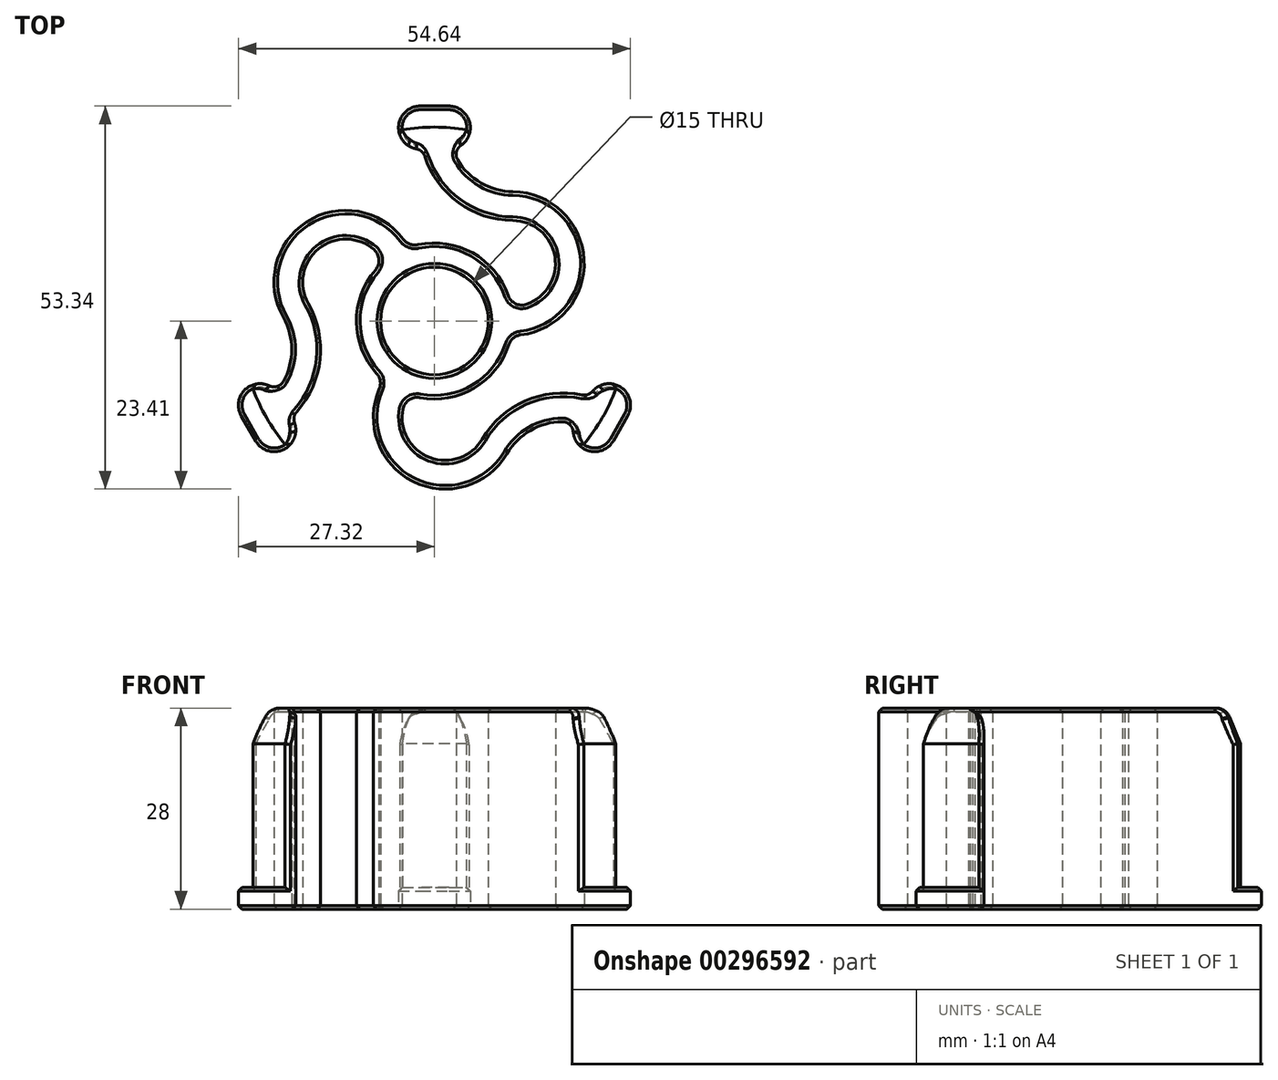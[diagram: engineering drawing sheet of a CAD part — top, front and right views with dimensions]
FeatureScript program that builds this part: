
annotation { "Feature Type Name" : "Feature", "Feature Type Description" : "" }
export const myFeature = defineFeature(function(context is Context, id is Id, definition is map)
    precondition{}
    {
        {
            var Q0;
            Q0=qCreatedBy(makeId("Top.planeOp"),FACE);
            var sketch = newSketch(context, id + "F0", { "sketchPlane" : qUnion([Q0])});
            skCircle(sketch, "E0", {"center": v(0, 0) * mm, "radius": 7.5 * mm});
            skArc(sketch, "E1", {"start": v(10.27, 3.56) * mm, "mid": v(5.32, 9.48) * mm, "end": v(-2.3, 10.62) * mm});
            skCircle(sketch, "E2", {"center": v(0, 0) * mm, "radius": 27 * mm, "construction": true});
            skArc(sketch, "E3", {"start": v(10.87, 0) * mm, "mid": v(18.87, 7.97) * mm, "end": v(10.92, 16) * mm, "construction": true});
            skLineSegment(sketch, "E4", {"start": v(0, 0) * mm, "end": v(0, 27) * mm, "construction": true});
            skArc(sketch, "E5", {"start": v(0, 27) * mm, "mid": v(3.2, 19.25) * mm, "end": v(10.92, 16) * mm, "construction": true});
            skLineSegment(sketch, "E6", {"start": v(10.87, 0) * mm, "end": v(0, 0) * mm, "construction": true});
            skArc(sketch, "E7.0", {"start": v(12.8, 2.32) * mm, "mid": v(16.79, 8.96) * mm, "end": v(10.9, 14) * mm});
            skArc(sketch, "E7.1", {"start": v(-1.36, 22.96) * mm, "mid": v(3.33, 16.5) * mm, "end": v(10.9, 14) * mm});
            skArc(sketch, "E8.0", {"start": v(12.02, -1.93) * mm, "mid": v(20.85, 8.54) * mm, "end": v(10.94, 18) * mm});
            skArc(sketch, "E8.1", {"start": v(3.24, 22.45) * mm, "mid": v(6.5, 19.2) * mm, "end": v(10.94, 18) * mm});
            skLineSegment(sketch, "E9", {"start": v(0, 27) * mm, "end": v(0, 32) * mm, "construction": true});
            skPoint(sketch, "E10.visualSharp", {"position": v(10.68, -2) * mm});
            skArc(sketch, "E10.filletArc", {"start": v(12.02, -1.93) * mm, "mid": v(10.98, -2.38) * mm, "end": v(10.35, -3.31) * mm});
            skPoint(sketch, "E11.visualSharp", {"position": v(10.68, 2) * mm});
            skArc(sketch, "E11.filletArc", {"start": v(10.27, 3.56) * mm, "mid": v(11.28, 2.42) * mm, "end": v(12.8, 2.32) * mm});
            skArc(sketch, "E12", {"start": v(-4.97, 26.54) * mm, "mid": v(-4.17, 24.85) * mm, "end": v(-2.52, 23.97) * mm});
            skArc(sketch, "E13", {"start": v(3.69, 24.45) * mm, "mid": v(4.56, 25.35) * mm, "end": v(4.98, 26.54) * mm});
            skArc(sketch, "E14", {"start": v(4.98, 26.54) * mm, "mid": v(0, 27) * mm, "end": v(-4.97, 26.54) * mm});
            skArc(sketch, "E15.1.0", {"start": v(-4.34, 11.38) * mm, "mid": v(-17.83, 13.79) * mm, "end": v(-21.06, 0.47) * mm});
            skArc(sketch, "E15.1.1", {"start": v(-8.22, 7.11) * mm, "mid": v(-7.73, 8.56) * mm, "end": v(-8.41, 9.93) * mm});
            skArc(sketch, "E15.1.2", {"start": v(-4.34, 11.38) * mm, "mid": v(-3.43, 10.7) * mm, "end": v(-2.3, 10.62) * mm});
            skArc(sketch, "E15.1.3", {"start": v(-8.41, 9.93) * mm, "mid": v(-16.15, 10.06) * mm, "end": v(-17.58, 2.45) * mm});
            skArc(sketch, "E15.1.4", {"start": v(-5.43, 9.41) * mm, "mid": v(-16.34, 12.35) * mm, "end": v(-19.32, 1.46) * mm, "construction": true});
            skArc(sketch, "E15.1.5", {"start": v(-23.38, -13.5) * mm, "mid": v(-18.27, -6.86) * mm, "end": v(-19.32, 1.46) * mm, "construction": true});
            skArc(sketch, "E15.1.6", {"start": v(-21.06, -8.42) * mm, "mid": v(-19.88, -3.97) * mm, "end": v(-21.06, 0.47) * mm});
            skArc(sketch, "E15.1.7", {"start": v(-19.2, -12.65) * mm, "mid": v(-15.96, -5.37) * mm, "end": v(-17.58, 2.45) * mm});
            skArc(sketch, "E15.1.8", {"start": v(-20.5, -17.58) * mm, "mid": v(-19.44, -16.04) * mm, "end": v(-19.5, -14.17) * mm});
            skArc(sketch, "E15.1.9", {"start": v(-23.01, -9.03) * mm, "mid": v(-24.23, -8.73) * mm, "end": v(-25.47, -8.96) * mm});
            skArc(sketch, "E15.1.10", {"start": v(-25.47, -8.96) * mm, "mid": v(-23.38, -13.5) * mm, "end": v(-20.5, -17.58) * mm});
            skArc(sketch, "E15.2.0", {"start": v(-7.69, -9.45) * mm, "mid": v(-3.03, -22.33) * mm, "end": v(10.12, -18.47) * mm});
            skArc(sketch, "E15.2.1", {"start": v(-2.05, -10.67) * mm, "mid": v(-3.55, -10.98) * mm, "end": v(-4.4, -12.25) * mm});
            skArc(sketch, "E15.2.2", {"start": v(-7.69, -9.45) * mm, "mid": v(-7.55, -8.32) * mm, "end": v(-8.04, -7.3) * mm});
            skArc(sketch, "E15.2.3", {"start": v(-4.4, -12.25) * mm, "mid": v(-0.63, -19.02) * mm, "end": v(6.67, -16.45) * mm});
            skArc(sketch, "E15.2.4", {"start": v(-5.43, -9.41) * mm, "mid": v(-2.53, -20.32) * mm, "end": v(8.4, -17.46) * mm, "construction": true});
            skArc(sketch, "E15.2.5", {"start": v(23.38, -13.5) * mm, "mid": v(15.07, -12.4) * mm, "end": v(8.4, -17.46) * mm, "construction": true});
            skArc(sketch, "E15.2.6", {"start": v(17.82, -14.03) * mm, "mid": v(13.38, -15.23) * mm, "end": v(10.12, -18.47) * mm});
            skArc(sketch, "E15.2.7", {"start": v(20.56, -10.3) * mm, "mid": v(12.63, -11.14) * mm, "end": v(6.67, -16.45) * mm});
            skArc(sketch, "E15.2.8", {"start": v(25.47, -8.96) * mm, "mid": v(23.6, -8.82) * mm, "end": v(22.02, -9.8) * mm});
            skArc(sketch, "E15.2.9", {"start": v(19.33, -15.42) * mm, "mid": v(19.68, -16.62) * mm, "end": v(20.5, -17.58) * mm});
            skArc(sketch, "E15.2.10", {"start": v(20.5, -17.58) * mm, "mid": v(23.38, -13.5) * mm, "end": v(25.47, -8.96) * mm});
            skLineSegment(sketch, "E16", {"start": v(-5.43, 9.41) * mm, "end": v(0, 0) * mm, "construction": true});
            skArc(sketch, "E17.trimOffspring", {"start": v(-8.22, 7.11) * mm, "mid": v(-10.87, -0.13) * mm, "end": v(-8.04, -7.3) * mm});
            skArc(sketch, "E18.trimOffspring", {"start": v(-2.05, -10.67) * mm, "mid": v(5.55, -9.34) * mm, "end": v(10.35, -3.31) * mm});
            skPoint(sketch, "E19.visualSharp", {"position": v(-19.92, -13.4) * mm});
            skArc(sketch, "E19.filletArc", {"start": v(-19.2, -12.65) * mm, "mid": v(-19.56, -13.37) * mm, "end": v(-19.5, -14.17) * mm});
            skPoint(sketch, "E20.visualSharp", {"position": v(-22.02, -9.8) * mm});
            skArc(sketch, "E20.filletArc", {"start": v(-23.01, -9.03) * mm, "mid": v(-21.92, -9.11) * mm, "end": v(-21.06, -8.42) * mm});
            skPoint(sketch, "E21.visualSharp", {"position": v(-1.64, 23.95) * mm});
            skArc(sketch, "E21.filletArc", {"start": v(-1.36, 22.96) * mm, "mid": v(-1.8, 23.63) * mm, "end": v(-2.52, 23.97) * mm});
            skPoint(sketch, "E22.visualSharp", {"position": v(2.52, 23.97) * mm});
            skArc(sketch, "E22.filletArc", {"start": v(3.69, 24.45) * mm, "mid": v(3.07, 23.53) * mm, "end": v(3.24, 22.45) * mm});
            skPoint(sketch, "E23.visualSharp", {"position": v(21.56, -10.56) * mm});
            skArc(sketch, "E23.filletArc", {"start": v(20.56, -10.3) * mm, "mid": v(21.36, -10.26) * mm, "end": v(22.02, -9.8) * mm});
            skPoint(sketch, "E24.visualSharp", {"position": v(19.5, -14.17) * mm});
            skArc(sketch, "E24.filletArc", {"start": v(19.33, -15.42) * mm, "mid": v(18.85, -14.42) * mm, "end": v(17.82, -14.03) * mm});
            skSolve(sketch);
        }
        {
            var Q0;
            Q0 = qSketchRegion(id + "F0", true);
            extrude(context, id + "F1", {"entities" : qUnion([Q0]), "depth" : 28 * mm});
        }
        {
            var Q0;
            Q0=makeQuery(id+"F1.opExtrude","CAP_FACE",FACE,{"disambiguationData":[OSD([sQuery(id+"F0.wireOp",EDGE,"E0"),sQuery(id+"F0.wireOp",EDGE,"E1"),sQuery(id+"F0.wireOp",EDGE,"E7.0"),sQuery(id+"F0.wireOp",EDGE,"E7.1"),sQuery(id+"F0.wireOp",EDGE,"E8.0"),sQuery(id+"F0.wireOp",EDGE,"E8.1"),sQuery(id+"F0.wireOp",EDGE,"E10.filletArc"),sQuery(id+"F0.wireOp",EDGE,"E11.filletArc"),sQuery(id+"F0.wireOp",EDGE,"E12"),sQuery(id+"F0.wireOp",EDGE,"E13"),sQuery(id+"F0.wireOp",EDGE,"E14"),sQuery(id+"F0.wireOp",EDGE,"E15.1.0"),sQuery(id+"F0.wireOp",EDGE,"E15.1.1"),sQuery(id+"F0.wireOp",EDGE,"E15.1.2"),sQuery(id+"F0.wireOp",EDGE,"E15.1.3"),sQuery(id+"F0.wireOp",EDGE,"E15.1.6"),sQuery(id+"F0.wireOp",EDGE,"E15.1.7"),sQuery(id+"F0.wireOp",EDGE,"E15.1.8"),sQuery(id+"F0.wireOp",EDGE,"E15.1.9"),sQuery(id+"F0.wireOp",EDGE,"E15.1.10"),sQuery(id+"F0.wireOp",EDGE,"E15.2.0"),sQuery(id+"F0.wireOp",EDGE,"E15.2.1"),sQuery(id+"F0.wireOp",EDGE,"E15.2.2"),sQuery(id+"F0.wireOp",EDGE,"E15.2.3"),sQuery(id+"F0.wireOp",EDGE,"E15.2.6"),sQuery(id+"F0.wireOp",EDGE,"E15.2.7"),sQuery(id+"F0.wireOp",EDGE,"E15.2.8"),sQuery(id+"F0.wireOp",EDGE,"E15.2.9"),sQuery(id+"F0.wireOp",EDGE,"E15.2.10"),sQuery(id+"F0.wireOp",EDGE,"E17.trimOffspring"),sQuery(id+"F0.wireOp",EDGE,"E18.trimOffspring")])],"isStart":true});
            var sketch = newSketch(context, id + "F2", { "sketchPlane" : qUnion([Q0])});
            skArc(sketch, "E25", {"start": v(-2, -23.93) * mm, "mid": v(-5, -26.93) * mm, "end": v(-2, -29.93) * mm});
            skArc(sketch, "E26", {"start": v(2, -29.93) * mm, "mid": v(5, -26.93) * mm, "end": v(2, -23.93) * mm});
            skLineSegment(sketch, "E27", {"start": v(-2, -29.93) * mm, "end": v(2, -29.93) * mm});
            skLineSegment(sketch, "E28", {"start": v(-2, -23.93) * mm, "end": v(2, -23.93) * mm});
            skLineSegment(sketch, "E29.1.0", {"start": v(26.92, 13.23) * mm, "end": v(24.92, 16.7) * mm});
            skLineSegment(sketch, "E29.1.1", {"start": v(21.72, 10.23) * mm, "end": v(19.72, 13.7) * mm});
            skArc(sketch, "E29.1.2", {"start": v(24.92, 16.7) * mm, "mid": v(20.82, 17.8) * mm, "end": v(19.72, 13.7) * mm});
            skArc(sketch, "E29.1.3", {"start": v(21.72, 10.23) * mm, "mid": v(25.82, 9.13) * mm, "end": v(26.92, 13.23) * mm});
            skLineSegment(sketch, "E29.2.0", {"start": v(-24.92, 16.7) * mm, "end": v(-26.92, 13.23) * mm});
            skLineSegment(sketch, "E29.2.1", {"start": v(-19.72, 13.7) * mm, "end": v(-21.72, 10.23) * mm});
            skArc(sketch, "E29.2.2", {"start": v(-26.92, 13.23) * mm, "mid": v(-25.82, 9.13) * mm, "end": v(-21.72, 10.23) * mm});
            skArc(sketch, "E29.2.3", {"start": v(-19.72, 13.7) * mm, "mid": v(-20.82, 17.8) * mm, "end": v(-24.92, 16.7) * mm});
            skPoint(sketch, "E29.center", {"position": v(0, 0) * mm});
            skLineSegment(sketch, "E30", {"start": v(0, 0) * mm, "end": v(-24.32, 11.73) * mm, "construction": true});
            skSolve(sketch);
        }
        {
            var Q0;
            Q0 = qSketchRegion(id + "F2", true);
            extrude(context, id + "F3", {"entities" : qUnion([Q0]), "operationType" : NewBodyOperationType.ADD, "oppositeDirection" : true, "depth" : 3 * mm});
        }
        {
            var Q0;
            Q0=makeQuery(id+"F1.opExtrude","CAP_EDGE",EDGE,{"disambiguationData":[OSD([sQuery(id+"F0.wireOp",EDGE,"E15.2.10")])],"isStart":false});
            var Q1;
            Q1=makeQuery(id+"F1.opExtrude","CAP_EDGE",EDGE,{"disambiguationData":[OSD([sQuery(id+"F0.wireOp",EDGE,"E15.1.10")])],"isStart":false});
            var Q2;
            Q2=makeQuery(id+"F1.opExtrude","CAP_EDGE",EDGE,{"disambiguationData":[OSD([sQuery(id+"F0.wireOp",EDGE,"E14")])],"isStart":false});
            chamfer(context, id + "F4", {"entities" : qUnion([Q0, Q1, Q2]), "chamferType" : ChamferType.TWO_OFFSETS, "width1" : 2 * mm, "oppositeDirection" : false, "width2" : 5 * mm, "tangentPropagation" : true});
        }
        {
            var Q0;
            {var subQ0=sQuery(id+"F0.wireOp",EDGE,"E15.2.10");Q0=makeQuery(id+"F4.opChamfer","BLEND_EDGE",EDGE,{"blendedFrom":[makeQuery(id+"F1.opExtrude","CAP_EDGE",EDGE,{"disambiguationData":[OSD([subQ0])],"isStart":false}),makeQuery(id+"F1.opExtrude","CAP_FACE",FACE,{"disambiguationData":[OSD([sQuery(id+"F0.wireOp",EDGE,"E0"),sQuery(id+"F0.wireOp",EDGE,"E1"),sQuery(id+"F0.wireOp",EDGE,"E7.0"),sQuery(id+"F0.wireOp",EDGE,"E7.1"),sQuery(id+"F0.wireOp",EDGE,"E8.0"),sQuery(id+"F0.wireOp",EDGE,"E8.1"),sQuery(id+"F0.wireOp",EDGE,"E10.filletArc"),sQuery(id+"F0.wireOp",EDGE,"E11.filletArc"),sQuery(id+"F0.wireOp",EDGE,"E12"),sQuery(id+"F0.wireOp",EDGE,"E13"),sQuery(id+"F0.wireOp",EDGE,"E14"),sQuery(id+"F0.wireOp",EDGE,"E15.1.0"),sQuery(id+"F0.wireOp",EDGE,"E15.1.1"),sQuery(id+"F0.wireOp",EDGE,"E15.1.2"),sQuery(id+"F0.wireOp",EDGE,"E15.1.3"),sQuery(id+"F0.wireOp",EDGE,"E15.1.6"),sQuery(id+"F0.wireOp",EDGE,"E15.1.7"),sQuery(id+"F0.wireOp",EDGE,"E15.1.8"),sQuery(id+"F0.wireOp",EDGE,"E15.1.9"),sQuery(id+"F0.wireOp",EDGE,"E15.1.10"),sQuery(id+"F0.wireOp",EDGE,"E15.2.0"),sQuery(id+"F0.wireOp",EDGE,"E15.2.1"),sQuery(id+"F0.wireOp",EDGE,"E15.2.2"),sQuery(id+"F0.wireOp",EDGE,"E15.2.3"),sQuery(id+"F0.wireOp",EDGE,"E15.2.6"),sQuery(id+"F0.wireOp",EDGE,"E15.2.7"),sQuery(id+"F0.wireOp",EDGE,"E15.2.8"),sQuery(id+"F0.wireOp",EDGE,"E15.2.9"),subQ0,sQuery(id+"F0.wireOp",EDGE,"E17.trimOffspring"),sQuery(id+"F0.wireOp",EDGE,"E18.trimOffspring"),sQuery(id+"F0.wireOp",EDGE,"E19.filletArc"),sQuery(id+"F0.wireOp",EDGE,"E20.filletArc"),sQuery(id+"F0.wireOp",EDGE,"E21.filletArc"),sQuery(id+"F0.wireOp",EDGE,"E22.filletArc"),sQuery(id+"F0.wireOp",EDGE,"E23.filletArc"),sQuery(id+"F0.wireOp",EDGE,"E24.filletArc")])],"isStart":false})],"blendedInto":[makeQuery(id+"F1.opExtrude","CAP_FACE",FACE,{"disambiguationData":[OSD([sQuery(id+"F0.wireOp",EDGE,"E0"),sQuery(id+"F0.wireOp",EDGE,"E1"),sQuery(id+"F0.wireOp",EDGE,"E7.0"),sQuery(id+"F0.wireOp",EDGE,"E7.1"),sQuery(id+"F0.wireOp",EDGE,"E8.0"),sQuery(id+"F0.wireOp",EDGE,"E8.1"),sQuery(id+"F0.wireOp",EDGE,"E10.filletArc"),sQuery(id+"F0.wireOp",EDGE,"E11.filletArc"),sQuery(id+"F0.wireOp",EDGE,"E12"),sQuery(id+"F0.wireOp",EDGE,"E13"),sQuery(id+"F0.wireOp",EDGE,"E14"),sQuery(id+"F0.wireOp",EDGE,"E15.1.0"),sQuery(id+"F0.wireOp",EDGE,"E15.1.1"),sQuery(id+"F0.wireOp",EDGE,"E15.1.2"),sQuery(id+"F0.wireOp",EDGE,"E15.1.3"),sQuery(id+"F0.wireOp",EDGE,"E15.1.6"),sQuery(id+"F0.wireOp",EDGE,"E15.1.7"),sQuery(id+"F0.wireOp",EDGE,"E15.1.8"),sQuery(id+"F0.wireOp",EDGE,"E15.1.9"),sQuery(id+"F0.wireOp",EDGE,"E15.1.10"),sQuery(id+"F0.wireOp",EDGE,"E15.2.0"),sQuery(id+"F0.wireOp",EDGE,"E15.2.1"),sQuery(id+"F0.wireOp",EDGE,"E15.2.2"),sQuery(id+"F0.wireOp",EDGE,"E15.2.3"),sQuery(id+"F0.wireOp",EDGE,"E15.2.6"),sQuery(id+"F0.wireOp",EDGE,"E15.2.7"),sQuery(id+"F0.wireOp",EDGE,"E15.2.8"),sQuery(id+"F0.wireOp",EDGE,"E15.2.9"),subQ0,sQuery(id+"F0.wireOp",EDGE,"E17.trimOffspring"),sQuery(id+"F0.wireOp",EDGE,"E18.trimOffspring"),sQuery(id+"F0.wireOp",EDGE,"E19.filletArc"),sQuery(id+"F0.wireOp",EDGE,"E20.filletArc"),sQuery(id+"F0.wireOp",EDGE,"E21.filletArc"),sQuery(id+"F0.wireOp",EDGE,"E22.filletArc"),sQuery(id+"F0.wireOp",EDGE,"E23.filletArc"),sQuery(id+"F0.wireOp",EDGE,"E24.filletArc")])],"isStart":false})]});}
            var Q1;
            {var subQ0=sQuery(id+"F0.wireOp",EDGE,"E15.1.10");Q1=makeQuery(id+"F4.opChamfer","BLEND_EDGE",EDGE,{"blendedFrom":[makeQuery(id+"F1.opExtrude","CAP_EDGE",EDGE,{"disambiguationData":[OSD([subQ0])],"isStart":false}),makeQuery(id+"F1.opExtrude","CAP_FACE",FACE,{"disambiguationData":[OSD([sQuery(id+"F0.wireOp",EDGE,"E0"),sQuery(id+"F0.wireOp",EDGE,"E1"),sQuery(id+"F0.wireOp",EDGE,"E7.0"),sQuery(id+"F0.wireOp",EDGE,"E7.1"),sQuery(id+"F0.wireOp",EDGE,"E8.0"),sQuery(id+"F0.wireOp",EDGE,"E8.1"),sQuery(id+"F0.wireOp",EDGE,"E10.filletArc"),sQuery(id+"F0.wireOp",EDGE,"E11.filletArc"),sQuery(id+"F0.wireOp",EDGE,"E12"),sQuery(id+"F0.wireOp",EDGE,"E13"),sQuery(id+"F0.wireOp",EDGE,"E14"),sQuery(id+"F0.wireOp",EDGE,"E15.1.0"),sQuery(id+"F0.wireOp",EDGE,"E15.1.1"),sQuery(id+"F0.wireOp",EDGE,"E15.1.2"),sQuery(id+"F0.wireOp",EDGE,"E15.1.3"),sQuery(id+"F0.wireOp",EDGE,"E15.1.6"),sQuery(id+"F0.wireOp",EDGE,"E15.1.7"),sQuery(id+"F0.wireOp",EDGE,"E15.1.8"),sQuery(id+"F0.wireOp",EDGE,"E15.1.9"),subQ0,sQuery(id+"F0.wireOp",EDGE,"E15.2.0"),sQuery(id+"F0.wireOp",EDGE,"E15.2.1"),sQuery(id+"F0.wireOp",EDGE,"E15.2.2"),sQuery(id+"F0.wireOp",EDGE,"E15.2.3"),sQuery(id+"F0.wireOp",EDGE,"E15.2.6"),sQuery(id+"F0.wireOp",EDGE,"E15.2.7"),sQuery(id+"F0.wireOp",EDGE,"E15.2.8"),sQuery(id+"F0.wireOp",EDGE,"E15.2.9"),sQuery(id+"F0.wireOp",EDGE,"E15.2.10"),sQuery(id+"F0.wireOp",EDGE,"E17.trimOffspring"),sQuery(id+"F0.wireOp",EDGE,"E18.trimOffspring"),sQuery(id+"F0.wireOp",EDGE,"E19.filletArc"),sQuery(id+"F0.wireOp",EDGE,"E20.filletArc"),sQuery(id+"F0.wireOp",EDGE,"E21.filletArc"),sQuery(id+"F0.wireOp",EDGE,"E22.filletArc"),sQuery(id+"F0.wireOp",EDGE,"E23.filletArc"),sQuery(id+"F0.wireOp",EDGE,"E24.filletArc")])],"isStart":false})],"blendedInto":[makeQuery(id+"F1.opExtrude","CAP_FACE",FACE,{"disambiguationData":[OSD([sQuery(id+"F0.wireOp",EDGE,"E0"),sQuery(id+"F0.wireOp",EDGE,"E1"),sQuery(id+"F0.wireOp",EDGE,"E7.0"),sQuery(id+"F0.wireOp",EDGE,"E7.1"),sQuery(id+"F0.wireOp",EDGE,"E8.0"),sQuery(id+"F0.wireOp",EDGE,"E8.1"),sQuery(id+"F0.wireOp",EDGE,"E10.filletArc"),sQuery(id+"F0.wireOp",EDGE,"E11.filletArc"),sQuery(id+"F0.wireOp",EDGE,"E12"),sQuery(id+"F0.wireOp",EDGE,"E13"),sQuery(id+"F0.wireOp",EDGE,"E14"),sQuery(id+"F0.wireOp",EDGE,"E15.1.0"),sQuery(id+"F0.wireOp",EDGE,"E15.1.1"),sQuery(id+"F0.wireOp",EDGE,"E15.1.2"),sQuery(id+"F0.wireOp",EDGE,"E15.1.3"),sQuery(id+"F0.wireOp",EDGE,"E15.1.6"),sQuery(id+"F0.wireOp",EDGE,"E15.1.7"),sQuery(id+"F0.wireOp",EDGE,"E15.1.8"),sQuery(id+"F0.wireOp",EDGE,"E15.1.9"),subQ0,sQuery(id+"F0.wireOp",EDGE,"E15.2.0"),sQuery(id+"F0.wireOp",EDGE,"E15.2.1"),sQuery(id+"F0.wireOp",EDGE,"E15.2.2"),sQuery(id+"F0.wireOp",EDGE,"E15.2.3"),sQuery(id+"F0.wireOp",EDGE,"E15.2.6"),sQuery(id+"F0.wireOp",EDGE,"E15.2.7"),sQuery(id+"F0.wireOp",EDGE,"E15.2.8"),sQuery(id+"F0.wireOp",EDGE,"E15.2.9"),sQuery(id+"F0.wireOp",EDGE,"E15.2.10"),sQuery(id+"F0.wireOp",EDGE,"E17.trimOffspring"),sQuery(id+"F0.wireOp",EDGE,"E18.trimOffspring"),sQuery(id+"F0.wireOp",EDGE,"E19.filletArc"),sQuery(id+"F0.wireOp",EDGE,"E20.filletArc"),sQuery(id+"F0.wireOp",EDGE,"E21.filletArc"),sQuery(id+"F0.wireOp",EDGE,"E22.filletArc"),sQuery(id+"F0.wireOp",EDGE,"E23.filletArc"),sQuery(id+"F0.wireOp",EDGE,"E24.filletArc")])],"isStart":false})]});}
            var Q2;
            {var subQ0=sQuery(id+"F0.wireOp",EDGE,"E14");Q2=makeQuery(id+"F4.opChamfer","BLEND_EDGE",EDGE,{"blendedFrom":[makeQuery(id+"F1.opExtrude","CAP_EDGE",EDGE,{"disambiguationData":[OSD([subQ0])],"isStart":false}),makeQuery(id+"F1.opExtrude","CAP_FACE",FACE,{"disambiguationData":[OSD([sQuery(id+"F0.wireOp",EDGE,"E0"),sQuery(id+"F0.wireOp",EDGE,"E1"),sQuery(id+"F0.wireOp",EDGE,"E7.0"),sQuery(id+"F0.wireOp",EDGE,"E7.1"),sQuery(id+"F0.wireOp",EDGE,"E8.0"),sQuery(id+"F0.wireOp",EDGE,"E8.1"),sQuery(id+"F0.wireOp",EDGE,"E10.filletArc"),sQuery(id+"F0.wireOp",EDGE,"E11.filletArc"),sQuery(id+"F0.wireOp",EDGE,"E12"),sQuery(id+"F0.wireOp",EDGE,"E13"),subQ0,sQuery(id+"F0.wireOp",EDGE,"E15.1.0"),sQuery(id+"F0.wireOp",EDGE,"E15.1.1"),sQuery(id+"F0.wireOp",EDGE,"E15.1.2"),sQuery(id+"F0.wireOp",EDGE,"E15.1.3"),sQuery(id+"F0.wireOp",EDGE,"E15.1.6"),sQuery(id+"F0.wireOp",EDGE,"E15.1.7"),sQuery(id+"F0.wireOp",EDGE,"E15.1.8"),sQuery(id+"F0.wireOp",EDGE,"E15.1.9"),sQuery(id+"F0.wireOp",EDGE,"E15.1.10"),sQuery(id+"F0.wireOp",EDGE,"E15.2.0"),sQuery(id+"F0.wireOp",EDGE,"E15.2.1"),sQuery(id+"F0.wireOp",EDGE,"E15.2.2"),sQuery(id+"F0.wireOp",EDGE,"E15.2.3"),sQuery(id+"F0.wireOp",EDGE,"E15.2.6"),sQuery(id+"F0.wireOp",EDGE,"E15.2.7"),sQuery(id+"F0.wireOp",EDGE,"E15.2.8"),sQuery(id+"F0.wireOp",EDGE,"E15.2.9"),sQuery(id+"F0.wireOp",EDGE,"E15.2.10"),sQuery(id+"F0.wireOp",EDGE,"E17.trimOffspring"),sQuery(id+"F0.wireOp",EDGE,"E18.trimOffspring"),sQuery(id+"F0.wireOp",EDGE,"E19.filletArc"),sQuery(id+"F0.wireOp",EDGE,"E20.filletArc"),sQuery(id+"F0.wireOp",EDGE,"E21.filletArc"),sQuery(id+"F0.wireOp",EDGE,"E22.filletArc"),sQuery(id+"F0.wireOp",EDGE,"E23.filletArc"),sQuery(id+"F0.wireOp",EDGE,"E24.filletArc")])],"isStart":false})],"blendedInto":[makeQuery(id+"F1.opExtrude","CAP_FACE",FACE,{"disambiguationData":[OSD([sQuery(id+"F0.wireOp",EDGE,"E0"),sQuery(id+"F0.wireOp",EDGE,"E1"),sQuery(id+"F0.wireOp",EDGE,"E7.0"),sQuery(id+"F0.wireOp",EDGE,"E7.1"),sQuery(id+"F0.wireOp",EDGE,"E8.0"),sQuery(id+"F0.wireOp",EDGE,"E8.1"),sQuery(id+"F0.wireOp",EDGE,"E10.filletArc"),sQuery(id+"F0.wireOp",EDGE,"E11.filletArc"),sQuery(id+"F0.wireOp",EDGE,"E12"),sQuery(id+"F0.wireOp",EDGE,"E13"),subQ0,sQuery(id+"F0.wireOp",EDGE,"E15.1.0"),sQuery(id+"F0.wireOp",EDGE,"E15.1.1"),sQuery(id+"F0.wireOp",EDGE,"E15.1.2"),sQuery(id+"F0.wireOp",EDGE,"E15.1.3"),sQuery(id+"F0.wireOp",EDGE,"E15.1.6"),sQuery(id+"F0.wireOp",EDGE,"E15.1.7"),sQuery(id+"F0.wireOp",EDGE,"E15.1.8"),sQuery(id+"F0.wireOp",EDGE,"E15.1.9"),sQuery(id+"F0.wireOp",EDGE,"E15.1.10"),sQuery(id+"F0.wireOp",EDGE,"E15.2.0"),sQuery(id+"F0.wireOp",EDGE,"E15.2.1"),sQuery(id+"F0.wireOp",EDGE,"E15.2.2"),sQuery(id+"F0.wireOp",EDGE,"E15.2.3"),sQuery(id+"F0.wireOp",EDGE,"E15.2.6"),sQuery(id+"F0.wireOp",EDGE,"E15.2.7"),sQuery(id+"F0.wireOp",EDGE,"E15.2.8"),sQuery(id+"F0.wireOp",EDGE,"E15.2.9"),sQuery(id+"F0.wireOp",EDGE,"E15.2.10"),sQuery(id+"F0.wireOp",EDGE,"E17.trimOffspring"),sQuery(id+"F0.wireOp",EDGE,"E18.trimOffspring"),sQuery(id+"F0.wireOp",EDGE,"E19.filletArc"),sQuery(id+"F0.wireOp",EDGE,"E20.filletArc"),sQuery(id+"F0.wireOp",EDGE,"E21.filletArc"),sQuery(id+"F0.wireOp",EDGE,"E22.filletArc"),sQuery(id+"F0.wireOp",EDGE,"E23.filletArc"),sQuery(id+"F0.wireOp",EDGE,"E24.filletArc")])],"isStart":false})]});}
            fillet(context, id + "F5", {"entities" : qUnion([Q0, Q1, Q2]), "radius" : 2 * mm, "tangentPropagation" : true, "allowEdgeOverflow" : false});
        }
        {
            var Q0;
            Q0=makeQuery(id+"F1.opExtrude","CAP_EDGE",EDGE,{"disambiguationData":[OSD([sQuery(id+"F0.wireOp",EDGE,"E18.trimOffspring")])],"isStart":true});
            var Q1;
            Q1=makeQuery(id+"F1.opExtrude","CAP_EDGE",EDGE,{"disambiguationData":[OSD([sQuery(id+"F0.wireOp",EDGE,"E0")])],"isStart":true});
            var Q2;
            Q2=makeQuery(id+"F1.opExtrude","CAP_EDGE",EDGE,{"disambiguationData":[OSD([sQuery(id+"F0.wireOp",EDGE,"E15.2.0")])],"isStart":false});
            var Q3;
            Q3=makeQuery(id+"F1.opExtrude","CAP_EDGE",EDGE,{"disambiguationData":[OSD([sQuery(id+"F0.wireOp",EDGE,"E18.trimOffspring")])],"isStart":false});
            var Q4;
            Q4=makeQuery(id+"F1.opExtrude","CAP_EDGE",EDGE,{"disambiguationData":[OSD([sQuery(id+"F0.wireOp",EDGE,"E0")])],"isStart":false});
            var Q5;
            Q5=makeQuery(id+"F1.opExtrude","CAP_EDGE",EDGE,{"disambiguationData":[OSD([sQuery(id+"F0.wireOp",EDGE,"E1")])],"isStart":false});
            var Q6;
            Q6=makeQuery(id+"F1.opExtrude","SWEPT_EDGE",EDGE,{"disambiguationData":[OSD([sQuery(id+"F0.wireOp",EDGE,"E15.2.9"),sQuery(id+"F0.wireOp",EDGE,"E15.2.10")])]});
            var Q7;
            Q7=makeQuery(id+"F3.opExtrude","CAP_EDGE",EDGE,{"disambiguationData":[OSD([sQuery(id+"F2.wireOp",EDGE,"E29.1.2")])],"isStart":false});
            var Q8;
            Q8=makeQuery(id+"F1.opExtrude","SWEPT_EDGE",EDGE,{"disambiguationData":[OSD([sQuery(id+"F0.wireOp",EDGE,"E15.2.8"),sQuery(id+"F0.wireOp",EDGE,"E15.2.10")])]});
            var Q9;
            Q9=makeQuery(id+"F1.opExtrude","SWEPT_EDGE",EDGE,{"disambiguationData":[OSD([sQuery(id+"F0.wireOp",EDGE,"E15.1.8"),sQuery(id+"F0.wireOp",EDGE,"E15.1.10")])]});
            var Q10;
            Q10=makeQuery(id+"F3.opExtrude","CAP_EDGE",EDGE,{"disambiguationData":[OSD([sQuery(id+"F2.wireOp",EDGE,"E29.2.3")])],"isStart":false});
            var Q11;
            Q11=makeQuery(id+"F1.opExtrude","SWEPT_EDGE",EDGE,{"disambiguationData":[OSD([sQuery(id+"F0.wireOp",EDGE,"E15.1.9"),sQuery(id+"F0.wireOp",EDGE,"E15.1.10")])]});
            var Q12;
            Q12=makeQuery(id+"F1.opExtrude","SWEPT_EDGE",EDGE,{"disambiguationData":[OSD([sQuery(id+"F0.wireOp",EDGE,"E12"),sQuery(id+"F0.wireOp",EDGE,"E14")])]});
            var Q13;
            Q13=makeQuery(id+"F3.opExtrude","CAP_EDGE",EDGE,{"disambiguationData":[OSD([sQuery(id+"F2.wireOp",EDGE,"E25")])],"isStart":false});
            var Q14;
            Q14=makeQuery(id+"F1.opExtrude","SWEPT_EDGE",EDGE,{"disambiguationData":[OSD([sQuery(id+"F0.wireOp",EDGE,"E13"),sQuery(id+"F0.wireOp",EDGE,"E14")])]});
            chamfer(context, id + "F6", {"entities" : qUnion([Q0, Q1, Q2, Q3, Q4, Q5, Q6, Q7, Q8, Q9, Q10, Q11, Q12, Q13, Q14]), "width" : 0.5 * mm, "tangentPropagation" : true});
        }
    });
